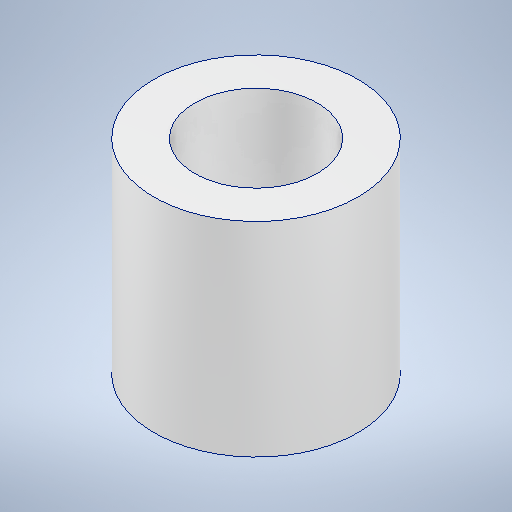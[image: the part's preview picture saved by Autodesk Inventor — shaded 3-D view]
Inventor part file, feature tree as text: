
AUTODESK INVENTOR PART (.ipt)
format: ipt  version: 2025 (Build 290162000, 162)  size: 227,840 bytes
history: native  units: mm
features: other x1, extrude x1, sketch x1
ambient origin geometry x8: Origin, YZ Plane, XZ Plane, XY Plane, X Axis, Y Axis, Z Axis, Center Point
bodies: Body1 (feature_tree)
feature tree (3):
  other  "Těleso1"
  extrude  "Vysunutí1"  Depth=3.0mm
  sketch  "Náčrt1"
